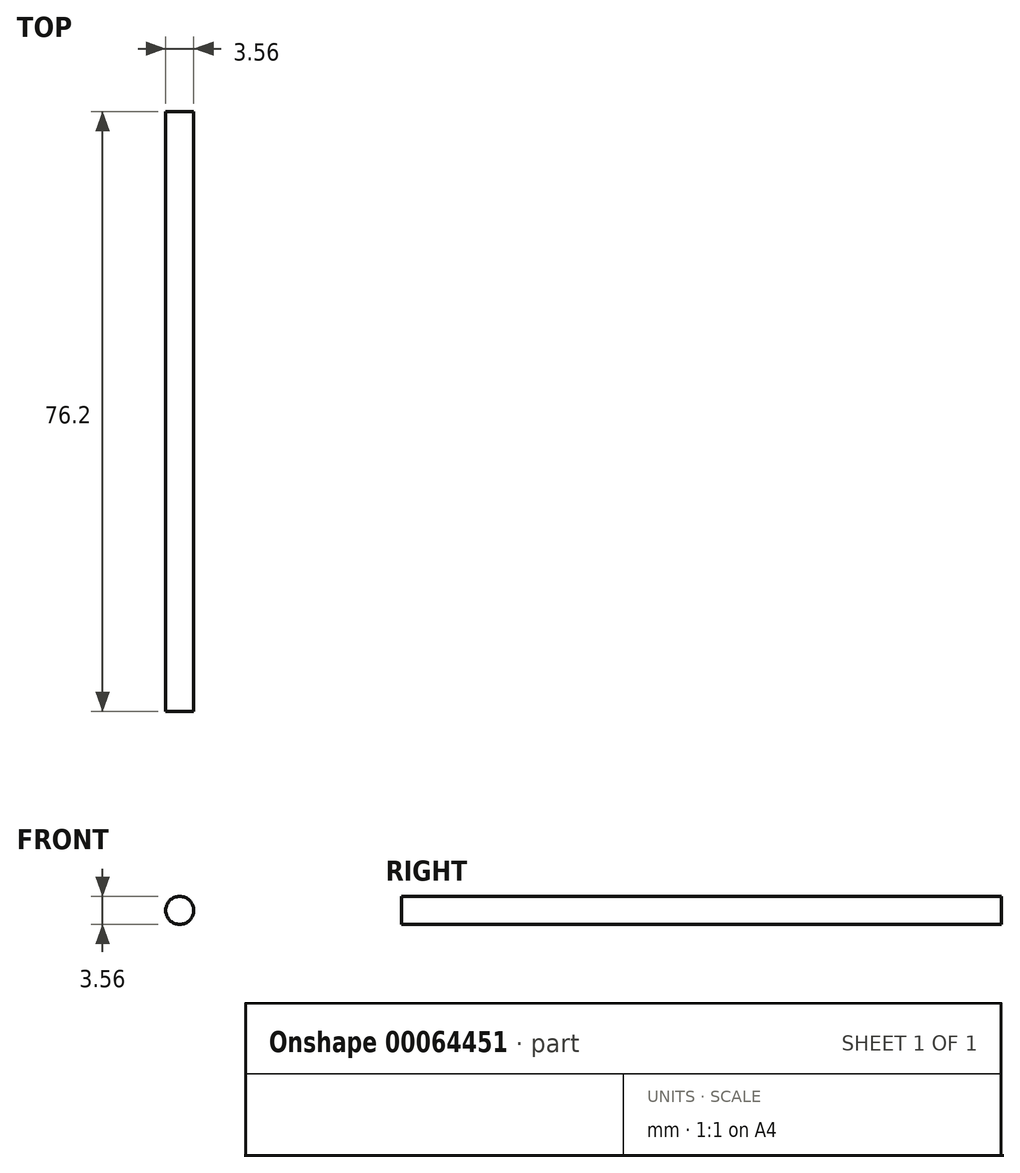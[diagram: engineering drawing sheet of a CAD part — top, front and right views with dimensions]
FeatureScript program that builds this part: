
annotation { "Feature Type Name" : "Feature", "Feature Type Description" : "" }
export const myFeature = defineFeature(function(context is Context, id is Id, definition is map)
    precondition{}
    {
        {
            var Q0;
            Q0=qCreatedBy(makeId("Front.planeOp"),FACE);
            var sketch = newSketch(context, id + "F0", { "sketchPlane" : qUnion([Q0])});
            skCircle(sketch, "E0", {"center": v(0, 0) * mm, "radius": 1.78 * mm});
            skSolve(sketch);
        }
        {
            var Q0;
            Q0 = qSketchRegion(id + "F0", true);
            extrude(context, id + "F1", {"entities" : qUnion([Q0]), "depth" : 76.2 * mm});
        }
    });
